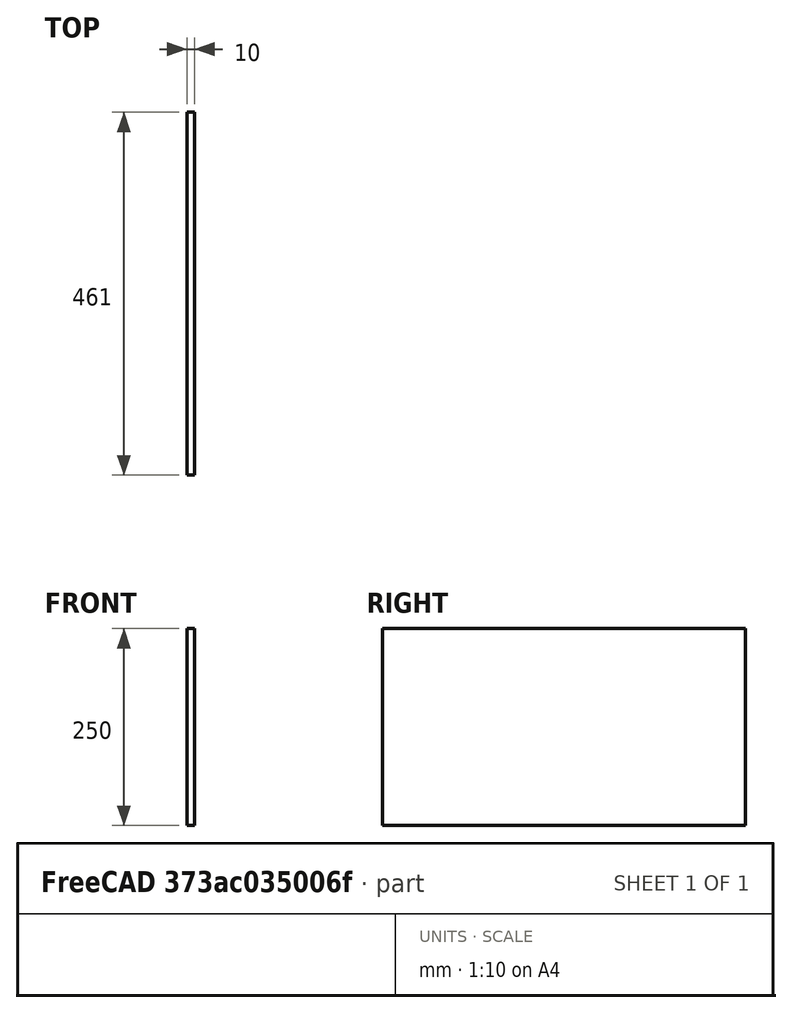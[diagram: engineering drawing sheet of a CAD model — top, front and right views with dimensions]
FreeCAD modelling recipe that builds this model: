
FCSTD DOCUMENT  (FreeCAD 0.18R16131 (Git))
Label: 500_pannel_electrical_YZ_1
License: All rights reserved
LicenseURL: http://en.wikipedia.org/wiki/All_rights_reserved
objects: Sketcher::SketchObject×1, Spreadsheet::Sheet×1, PartDesign::Pad×1, PartDesign::Body×1
note: 4 computed .brp shape members not serialized (recipe doc carries the construction recipe); baked Part::Feature solids carry a one-line shape summary decoded from their .brp

FEATURE [Sketcher::SketchObject] Sketch
  MapMode = 4
  Placement = pos=(0,0,0) rot=(0.57735,0.57735,0.57735;2.0944rad)
  Support = -> [XY_Plane]
  expr: Constraints[6] = Spreadsheet.nY
  expr: Constraints[5] = Spreadsheet.nZ
  sketch-geometry (5):
    g0: LineSegment StartX=0 StartY=0 StartZ=0 EndX=0 EndY=250 EndZ=0
    g1: LineSegment StartX=461 StartY=0 StartZ=0 EndX=461 EndY=250 EndZ=0
    g2: LineSegment StartX=461 StartY=250 StartZ=0 EndX=0 EndY=250 EndZ=0
    g3: LineSegment StartX=230.5 StartY=0 StartZ=0 EndX=0 EndY=0 EndZ=0
    g4: LineSegment StartX=461 StartY=0 StartZ=0 EndX=230.5 EndY=0 EndZ=0
  constraints (14):
    c: Vertical(g0)
    c: Vertical(g1)
    c: Coincident(g2,g1)
    c: Coincident(g2,g0)
    c: Horizontal(g2)
    c: DistanceY(g1,g1) = 250
    c: DistanceX(g2,g2) = 461
    c: Coincident(g3,g0)
    c: Coincident(g4,g1)
    c: Horizontal(g4)
    c: Equal(g3,g4)
    c: Coincident(g4,g3)
    c: Horizontal(g3)
    c: Coincident(g0,g-1)
FEATURE [Spreadsheet::Sheet] Spreadsheet  label="xls"
  cells = B7=KEYBOARD FRONT; B8=Width; C8=nY; D8(nY)==480 - 19; B9=Height; C9=nZ; D9(nZ)=250; E9=F(T); B10=Thickness; C10=nT; D10(nT)=10
FEATURE [PartDesign::Pad] Pad
  Length = 10
  Length2 = 100
  Profile = -> Sketch
  Reversed = true
  Type = 0
  expr: Length = Spreadsheet.nT
FEATURE [PartDesign::Body] Body
  Group = -> [Sketch,Pad]
  Origin = -> Origin
  Tip = -> Pad
